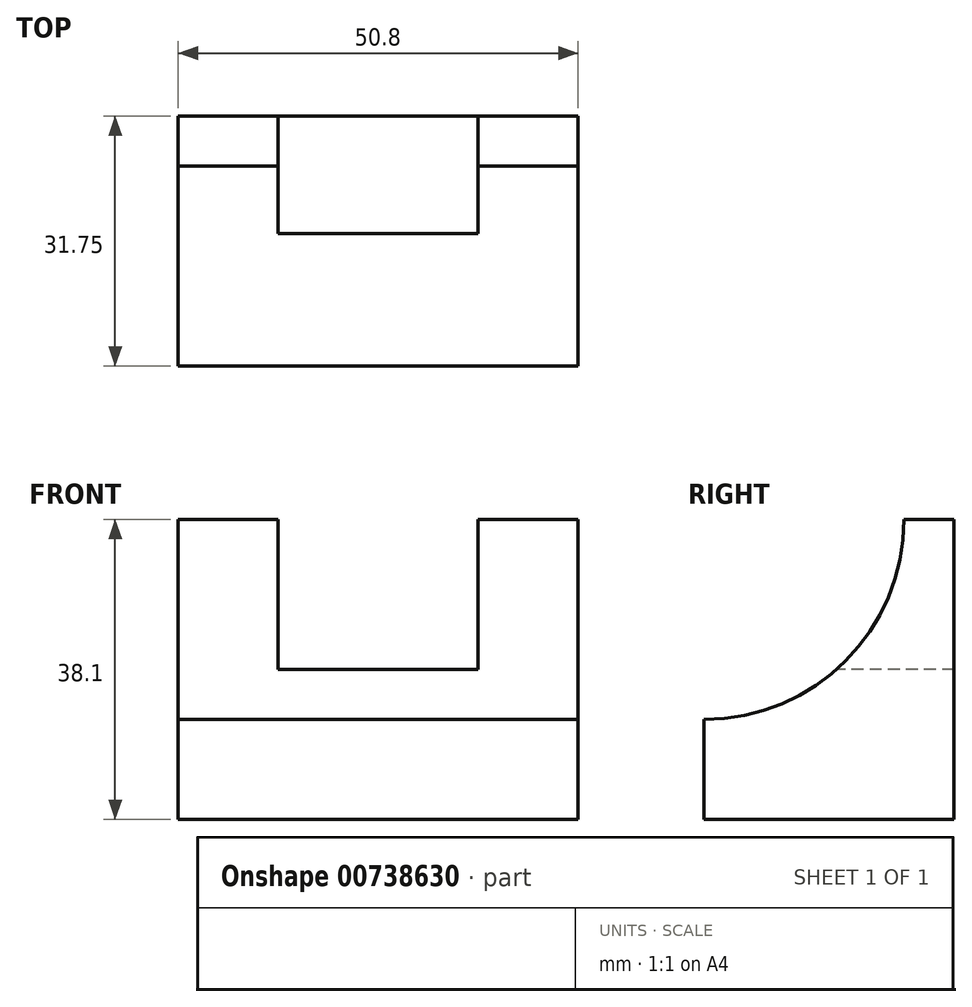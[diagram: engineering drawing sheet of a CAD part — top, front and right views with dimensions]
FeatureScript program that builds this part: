
annotation { "Feature Type Name" : "Feature", "Feature Type Description" : "" }
export const myFeature = defineFeature(function(context is Context, id is Id, definition is map)
    precondition{}
    {
        {
            var Q0;
            Q0=qCreatedBy(makeId("Right.planeOp"),FACE);
            var sketch = newSketch(context, id + "F0", { "sketchPlane" : qUnion([Q0])});
            skLineSegment(sketch, "E0.bottom", {"start": v(0, 0) * mm, "end": v(31.75, 0) * mm});
            skLineSegment(sketch, "E0.top", {"start": v(0, 38.1) * mm, "end": v(31.75, 38.1) * mm});
            skLineSegment(sketch, "E0.left", {"start": v(0, 0) * mm, "end": v(0, 38.1) * mm});
            skLineSegment(sketch, "E0.right", {"start": v(31.75, 0) * mm, "end": v(31.75, 38.1) * mm});
            skLineSegment(sketch, "E1", {"start": v(0, 0) * mm, "end": v(0, 12.7) * mm});
            skLineSegment(sketch, "E2", {"start": v(31.75, 38.1) * mm, "end": v(25.4, 38.1) * mm});
            skArc(sketch, "E3", {"start": v(0, 12.7) * mm, "mid": v(17.96, 20.14) * mm, "end": v(25.4, 38.1) * mm});
            skSolve(sketch);
        }
        {
            var Q0;
            {var subQ1=sQuery(id+"F0.wireOp",EDGE,"E0.bottom");Q0=makeQuery(id+"F0.imprint","IMPRINT",FACE,{"disambiguationData":[TD([[makeQuery(id+"F0.imprint","IMPRINT",EDGE,{"derivedFrom":subQ1}),1.0]])]});}
            extrude(context, id + "F1", {"entities" : qUnion([Q0]), "oppositeDirection" : true, "depth" : 50.8 * mm, "offsetDistance" : 25.4 * mm});
        }
        {
            var Q0;
            Q0=makeQuery(id+"F1.opExtrude","SWEPT_FACE",FACE,{"disambiguationData":[OSD([sQuery(id+"F0.wireOp",EDGE,"E0.top")])]});
            var sketch = newSketch(context, id + "F2", { "sketchPlane" : qUnion([Q0])});
            skLineSegment(sketch, "E4", {"start": v(-50.8, 31.75) * mm, "end": v(-38.1, 31.75) * mm});
            skLineSegment(sketch, "E5", {"start": v(-38.1, 31.75) * mm, "end": v(-12.7, 31.75) * mm});
            skLineSegment(sketch, "E6.top", {"start": v(-38.1, 11.06) * mm, "end": v(-12.7, 11.06) * mm});
            skLineSegment(sketch, "E6.left", {"start": v(-38.1, 31.75) * mm, "end": v(-38.1, 11.06) * mm});
            skLineSegment(sketch, "E6.right", {"start": v(-12.7, 31.75) * mm, "end": v(-12.7, 11.06) * mm});
            skSolve(sketch);
        }
        {
            var Q0;
            {var subQ0=sQuery(id+"F2.wireOp",EDGE,"E6.top");Q0=makeQuery(id+"F2.imprint","IMPRINT",FACE,{"disambiguationData":[TD([[makeQuery(id+"F2.imprint","IMPRINT",EDGE,{"derivedFrom":subQ0}),1.0]])]});}
            var Q1;
            {var subQ0=sQuery(id+"F2.wireOp",EDGE,"E5");Q1=makeQuery(id+"F2.imprint","IMPRINT",FACE,{"disambiguationData":[TD([[makeQuery(id+"F2.imprint","IMPRINT",EDGE,{"derivedFrom":subQ0}),-1.0]])]});}
            extrude(context, id + "F3", {"entities" : qUnion([Q0, Q1]), "operationType" : NewBodyOperationType.REMOVE, "oppositeDirection" : true, "depth" : 19.05 * mm, "offsetDistance" : 25.4 * mm});
        }
    });
